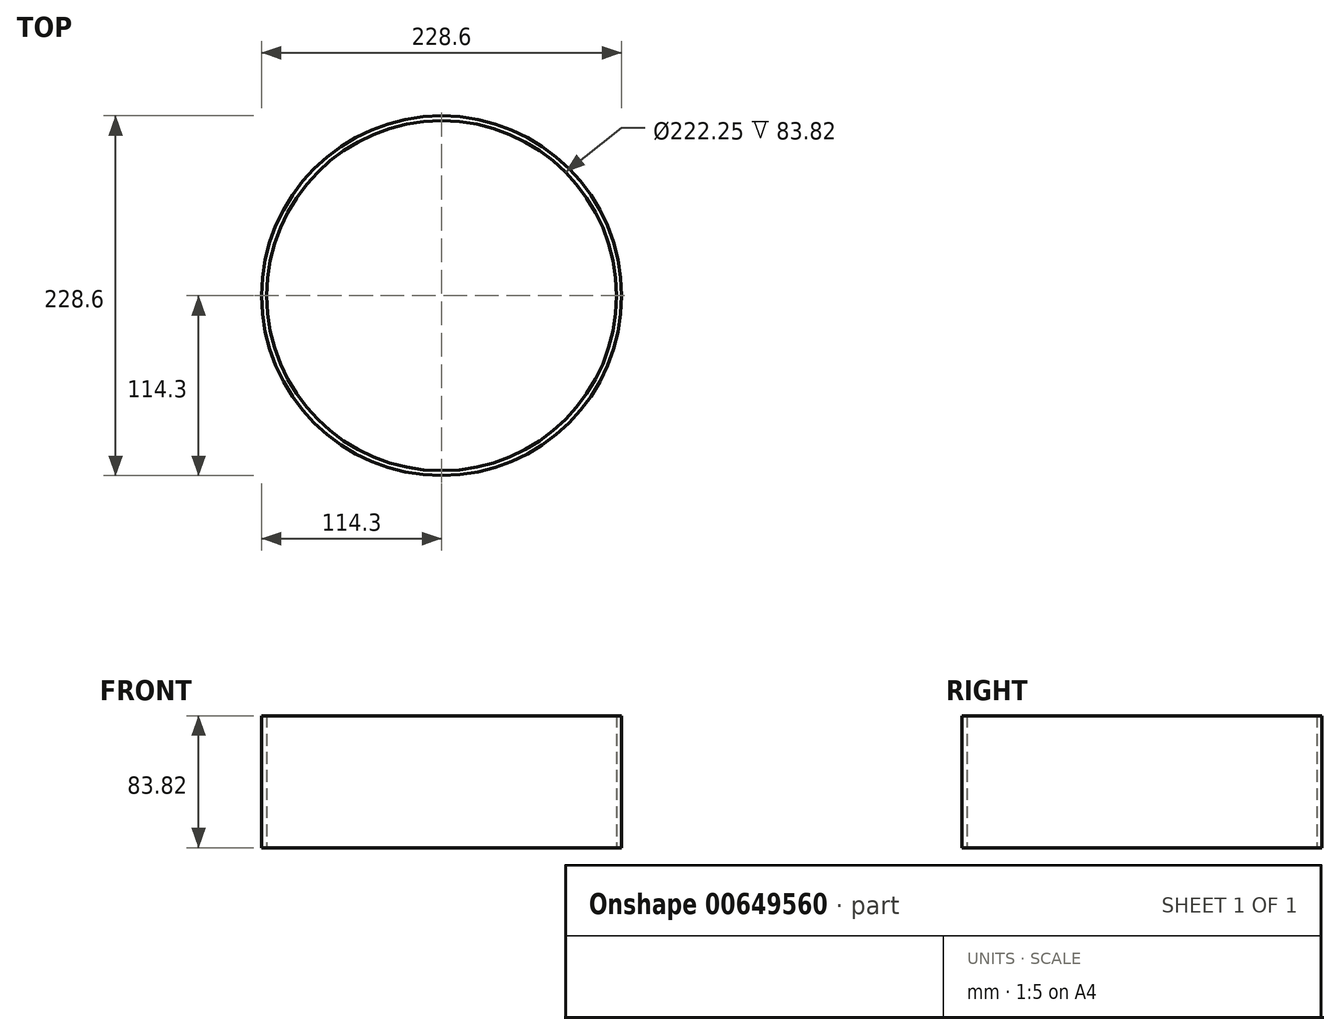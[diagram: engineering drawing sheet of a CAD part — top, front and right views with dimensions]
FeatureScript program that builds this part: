
annotation { "Feature Type Name" : "Feature", "Feature Type Description" : "" }
export const myFeature = defineFeature(function(context is Context, id is Id, definition is map)
    precondition{}
    {
        {
            var Q0;
            Q0=qCreatedBy(makeId("Top.planeOp"), FACE);
            var sketch = newSketch(context, id + "F0", { "sketchPlane" : qUnion([Q0])});
            skCircle(sketch, "E0", {"center": v(0, 0) * mm, "radius": 114.3 * mm});
            skCircle(sketch, "E1", {"center": v(0, 0) * mm, "radius": 111.13 * mm});
            skSolve(sketch);
        }
        {
            var Q0;
            Q0 = qSketchRegion(id + "F0", true);
            extrude(context, id + "F1", {"entities" : qUnion([Q0]), "depth" : 83.82 * mm, "offsetDistance" : 25.4 * mm});
        }
    });
